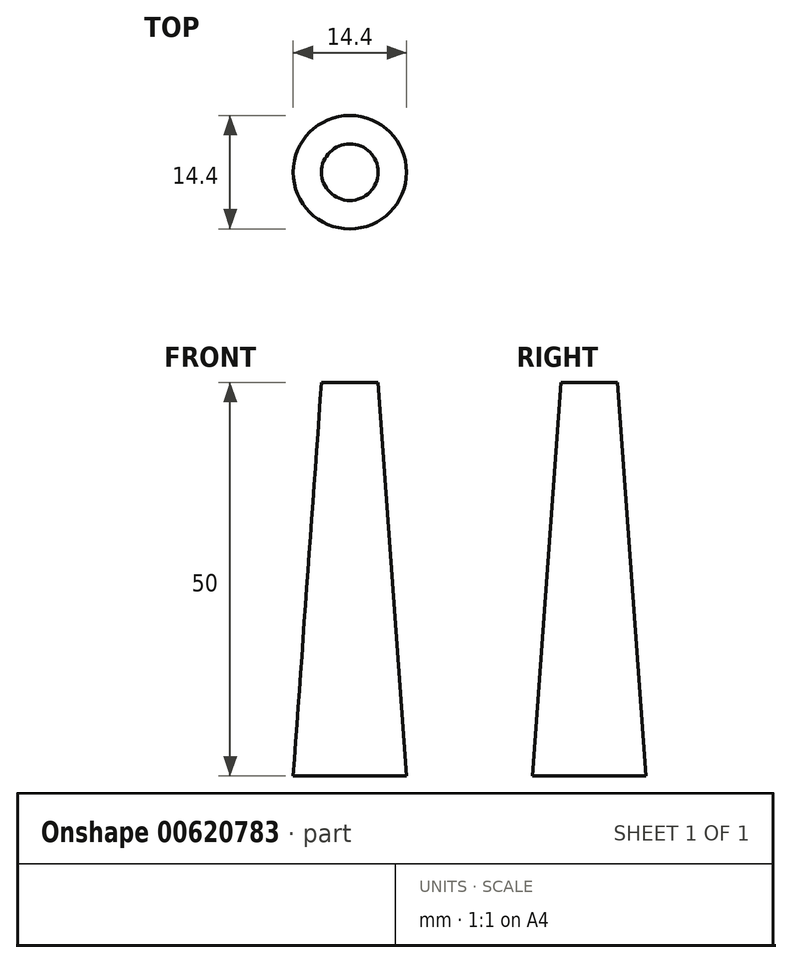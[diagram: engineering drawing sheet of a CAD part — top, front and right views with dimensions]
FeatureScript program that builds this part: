
annotation { "Feature Type Name" : "Feature", "Feature Type Description" : "" }
export const myFeature = defineFeature(function(context is Context, id is Id, definition is map)
    precondition{}
    {
        {
            var Q0;
            Q0=qCreatedBy(makeId("Front.planeOp"),FACE);
            var sketch = newSketch(context, id + "F0", { "sketchPlane" : qUnion([Q0])});
            skLineSegment(sketch, "E0", {"start": v(0, -25) * mm, "end": v(0, 25) * mm});
            skLineSegment(sketch, "E1", {"start": v(0, 25) * mm, "end": v(-3.6, 25) * mm});
            skLineSegment(sketch, "E2", {"start": v(0, -25) * mm, "end": v(-7.2, -25) * mm});
            skLineSegment(sketch, "E3", {"start": v(-3.6, 25) * mm, "end": v(-7.2, -25) * mm});
            skSolve(sketch);
        }
        {
            var Q0;
            Q0 = qSketchRegion(id + "F0", true);
            var Q1;
            Q1=sQuery(id+"F0.wireOp",EDGE,"E0");
            revolve(context, id + "F1", {"surfaceOperationType" : NewSurfaceOperationType.NEW, "entities" : qUnion([Q0]), "axis" : qUnion([Q1]), "revolveType" : RevolveType.FULL});
        }
    });
